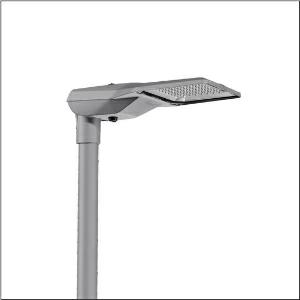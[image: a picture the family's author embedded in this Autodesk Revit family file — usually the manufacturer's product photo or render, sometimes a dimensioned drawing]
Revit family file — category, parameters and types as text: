
# Revit family: streetlight_sl_21_midi___st1_0ab_5xe3m33t08nb_9bc9
name_source: partatom
category: Lighting Fixtures
units: mm (PartAtom-declared; Revit-internal decimal feet)

## family parameters
Cut with Voids When Loaded = No
Host = Face
Light Source = No
Part Type = Normal
Room Calculation Point = No
Round Connector Dimension = Use Diameter
Shared = No

## types (1)
- --- (1 x LED, 19980 lm, 151.2 W, 3000K)
    Apparent Load = 151 VA
    CIE Flux Codes = 40 74 97 100 100
    Color Rendering = 70
    Color Temperature = 3000K
    Default Elevation = 1800 mm
    Description = Streetlight SL 21 midi, mast luminaire, primary light control with lens, of PMMA, primary optical cover: cover, of toughened safety glass, transparent, light distribution: ST1.0aB, light emission: direct distribution, primary light characteristic: asymmetric, installation type: side-entry, post-top, LED, High Power LED, rated luminous flux: 19.980lm, luminous efficacy: 132lm/W, light colour: 730, colour temperature: 3000K, control gear: D4i, control: flexible luminous flux parameterisation, time-dependent luminous flux control, constant luminous flux control, overheat protection, pre-setting: logarithmic dimming characteristic, mains connection: 230..240V, AC, 50/60Hz, start of lifetime: 151W, end of service life: 157W, reduction: 70W, luminaire housing, of diecast aluminium, powder-coated, Siteco® metallic grey (DB 702S), corrosivity category C5 high according to DIN EN ISO 12944, please order mast flange separately, inclination adjustable: 0°, 5°, 10°, 15°, sealing non-destructively replaceable, multi-level sealing system, length: 644mm, width: 335mm, height: 110mm, mast flange for spigot size: 42mm (side-entry): 5XC10008XM4, 60/48mm (side-entry/post-top): 5XC10108XM2, 76/60mm (side-entry/post-top): 5XC10108XM1, mounting height: 4..8m, Smart Interface below and above, protection rating (complete): IP66, insulation class (complete): insulation class II (safety insulation), certification: CE, ENEC, ENEC+, VDE, impact resistance: IK10, permissible operating ambient temperature for outdoor applications: -40..+50°C, standard-compliant lighting for roads and squares, packaging unit: 1 piece

Light Distribution: ST1.0aB
    Height = 111 mm
    Lamp = 1 x LED
    Lamp Light Flux = 19980 lm
    Lamp Power = 151.2 W
    Lamp count = 1
    Length = 644 mm
    Luminous efficacy = 132 lm/W
    Manufacturer = Siteco
    ModVariant = No
    Model = 5XE3M33T08NB
    Number of Poles = 1
    OnlyDefault = Yes
    Power Factor = 1
    Product Name = Streetlight SL 21 midi | ST1.0aB
    Product group = mast luminaire | pylon top
    ProductGroupID = 6100
    Protection Class = Protection class II
    Protection Degree = IP 66
    RLX_Detail_Level = 1
    RLX_Emergency_Light_Flux = 0 lm
    RLX_Emergency_Type = 0
    RLX_Emergency_Type_DB = No
    RlxData = <blob elided: 27049 chars, md5=e69465ae>
    Socket = socket
    Standby Power = 0 W
    System Light Flux = 19980 lm
    System Power = 151 W
    Type Comments = factory setting: luminous flux: 100 % | dim-lin: 254 | 802 mA
    Type Image = l_1004304.jpg
    URL = http://relux.com
    VarID = @adj_171367
    Voltage = 0 V
    Weight = 0.00 kg
    Width = 336 mm

## geometry (parser evidence)
native form markers: Blend x4, Sweep x10
no freeform markers — native parametric forms only
